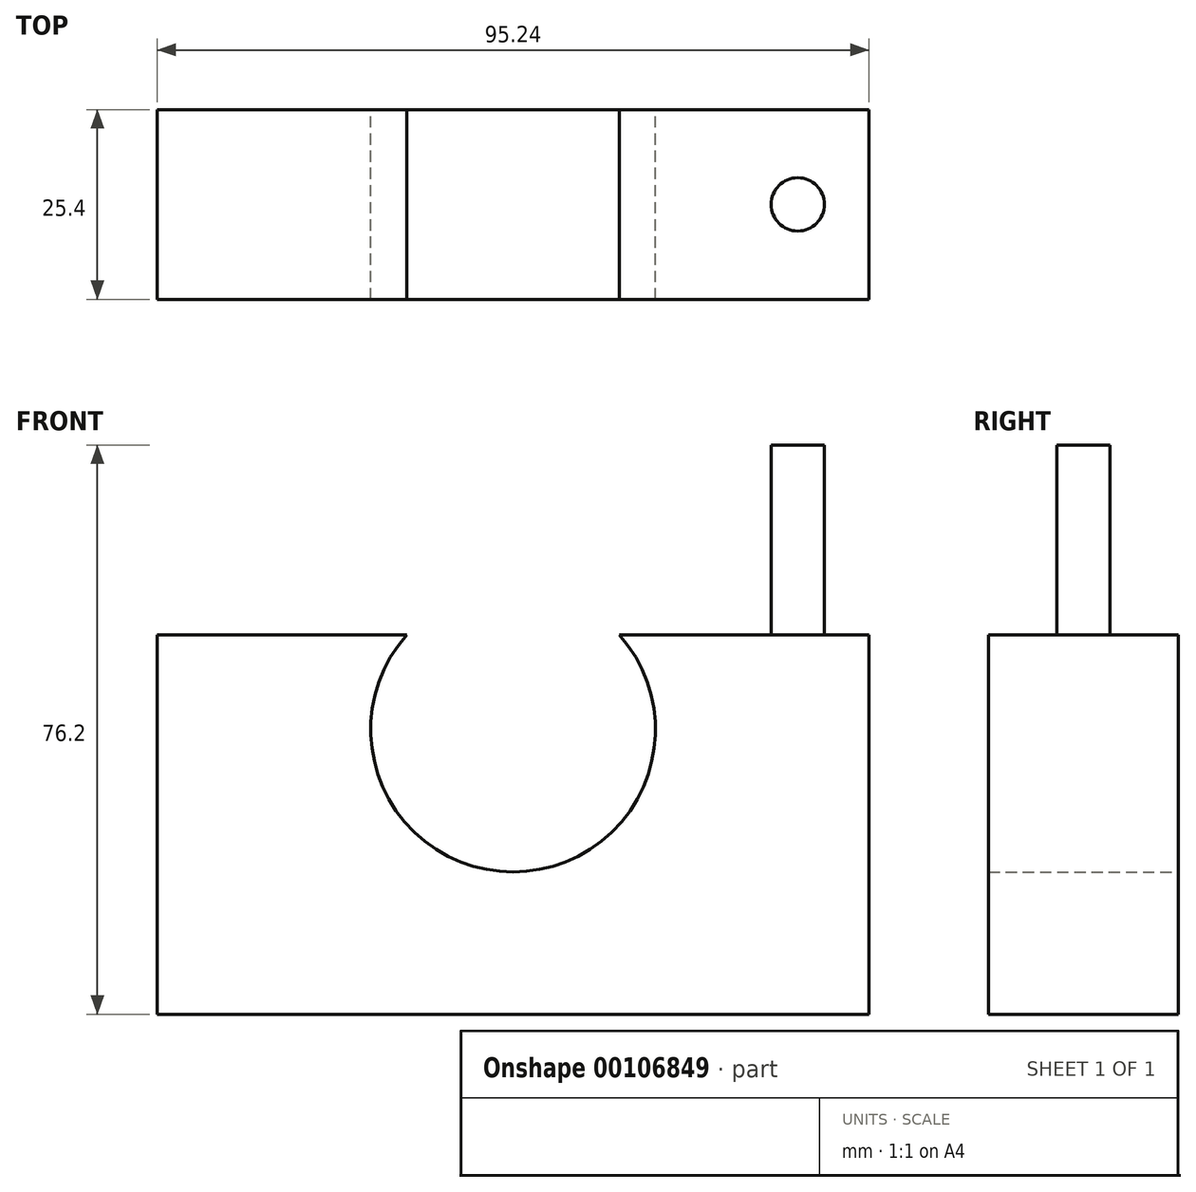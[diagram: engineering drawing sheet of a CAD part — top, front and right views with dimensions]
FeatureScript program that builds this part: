
annotation { "Feature Type Name" : "Feature", "Feature Type Description" : "" }
export const myFeature = defineFeature(function(context is Context, id is Id, definition is map)
    precondition{}
    {
        {
            var Q0;
            Q0=qCreatedBy(makeId("Front.planeOp"),FACE);
            var sketch = newSketch(context, id + "F0", { "sketchPlane" : qUnion([Q0])});
            skLineSegment(sketch, "E0.bottom", {"start": v(47.63, -38.1) * mm, "end": v(-47.62, -38.1) * mm});
            skLineSegment(sketch, "E0.top", {"start": v(47.63, 38.1) * mm, "end": v(-47.62, 38.1) * mm});
            skLineSegment(sketch, "E0.left", {"start": v(47.63, -38.1) * mm, "end": v(47.63, 38.1) * mm});
            skLineSegment(sketch, "E0.right", {"start": v(-47.62, -38.1) * mm, "end": v(-47.62, 38.1) * mm});
            skPoint(sketch, "E0.middle", {"position": v(0, 0) * mm});
            skCircle(sketch, "E1", {"center": v(0, 0) * mm, "radius": 19.05 * mm});
            skSolve(sketch);
        }
        {
            var Q0;
            Q0 = qSketchRegion(id + "F0", true);
            extrude(context, id + "F1", {"entities" : qUnion([Q0]), "depth" : 25.4 * mm});
        }
        {
            var Q0;
            Q0=makeQuery(id+"F1.opExtrude","SWEPT_FACE",FACE,{"disambiguationData":[OSD([sQuery(id+"F0.wireOp",EDGE,"E0.top")])]});
            var sketch = newSketch(context, id + "F2", { "sketchPlane" : qUnion([Q0])});
            skCircle(sketch, "E2", {"center": v(-38.1, -12.7) * mm, "radius": 3.57 * mm});
            skLineSegment(sketch, "E3", {"start": v(0, 0) * mm, "end": v(0, -25.72) * mm, "construction": true});
            skCircle(sketch, "E4.MirrorC", {"center": v(38.1, -12.7) * mm, "radius": 3.57 * mm});
            skSolve(sketch);
        }
        {
            var Q0;
            Q0=makeQuery(id+"F2.imprint","IMPRINT",FACE,{"disambiguationData":[TD([[makeQuery(id+"F2.imprint","IMPRINT",EDGE,{"derivedFrom":sQuery(id+"F2.wireOp",EDGE,"E4.MirrorC")}),-1.0]])]});
            var Q1;
            Q1=makeQuery(id+"F2.imprint","IMPRINT",FACE,{"disambiguationData":[TD([[makeQuery(id+"F2.imprint","IMPRINT",EDGE,{"derivedFrom":sQuery(id+"F2.wireOp",EDGE,"E2")}),1.0]])]});
            extrude(context, id + "F3", {"entities" : qUnion([Q0, Q1]), "operationType" : NewBodyOperationType.REMOVE, "oppositeDirection" : true, "depth" : 25.4 * mm});
        }
    });
